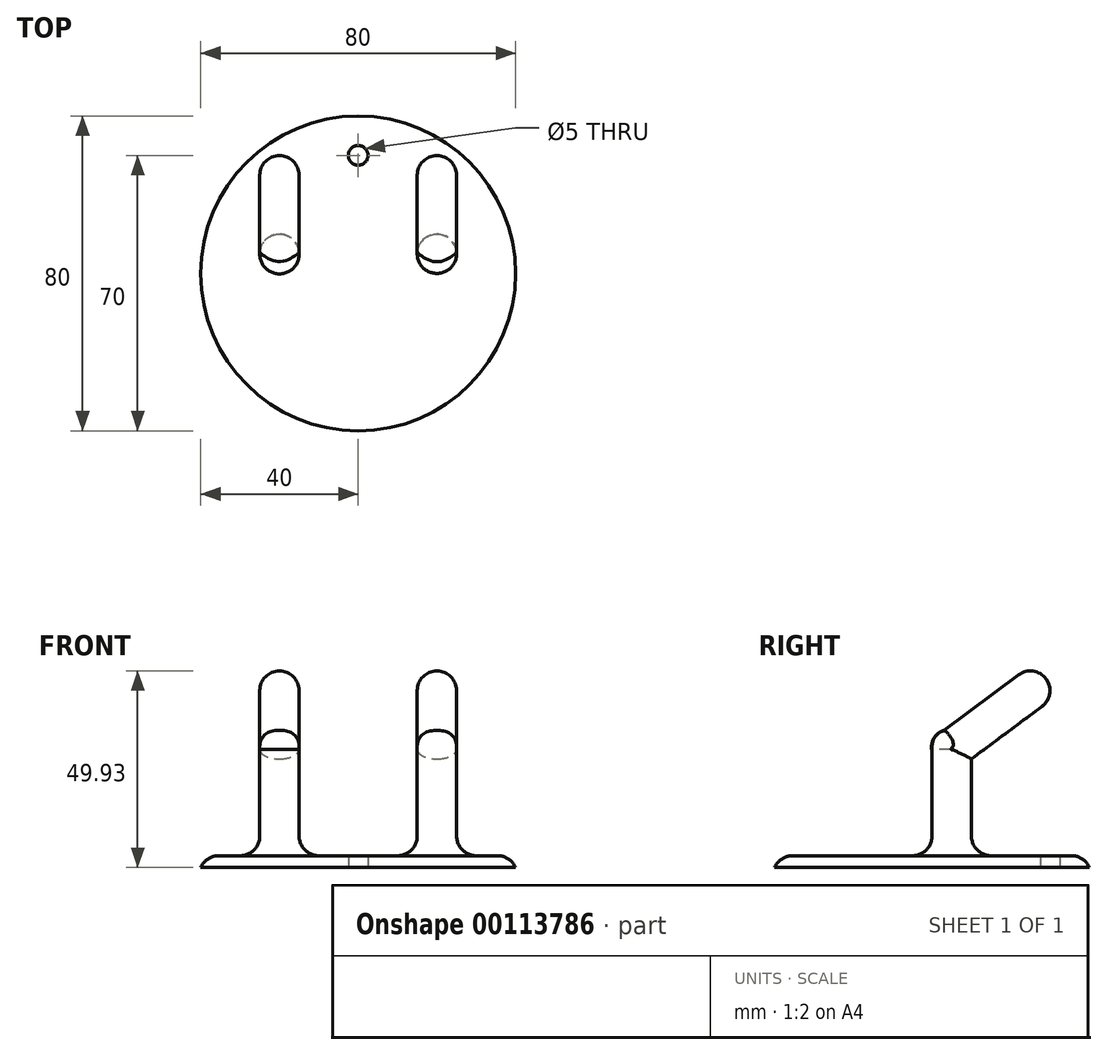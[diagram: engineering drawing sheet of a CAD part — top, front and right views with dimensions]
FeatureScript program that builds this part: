
annotation { "Feature Type Name" : "Feature", "Feature Type Description" : "" }
export const myFeature = defineFeature(function(context is Context, id is Id, definition is map)
    precondition{}
    {
        {
            var Q0;
            Q0=qCreatedBy(makeId("Top.planeOp"),FACE);
            var sketch = newSketch(context, id + "F0", { "sketchPlane" : qUnion([Q0])});
            skCircle(sketch, "E0", {"center": v(0, 0) * mm, "radius": 40 * mm});
            skLineSegment(sketch, "E1", {"start": v(-40, 0) * mm, "end": v(40, 0) * mm});
            skLineSegment(sketch, "E2", {"start": v(-39.69, 5) * mm, "end": v(39.69, 5) * mm});
            skSolve(sketch);
        }
        {
            var Q0;
            {var subQ0=sQuery(id+"F0.wireOp",EDGE,"E2");Q0=makeQuery(id+"F0.imprint","IMPRINT",FACE,{"disambiguationData":[TD([[makeQuery(id+"F0.imprint","IMPRINT",EDGE,{"derivedFrom":subQ0}),1.0]])]});}
            var sketch = newSketch(context, id + "F1", { "sketchPlane" : qUnion([Q0])});
            skCircle(sketch, "E3", {"center": v(-20, 5) * mm, "radius": 5 * mm});
            skCircle(sketch, "E4", {"center": v(20, 5) * mm, "radius": 5 * mm});
            skSolve(sketch);
        }
        {
            var Q0;
            {var subQ0=sQuery(id+"F0.wireOp",EDGE,"E2");Q0=makeQuery(id+"F0.imprint","IMPRINT",FACE,{"disambiguationData":[TD([[makeQuery(id+"F0.imprint","IMPRINT",EDGE,{"derivedFrom":subQ0}),1.0]])]});}
            var sketch = newSketch(context, id + "F2", { "sketchPlane" : qUnion([Q0])});
            skCircle(sketch, "E5", {"center": v(0, 30) * mm, "radius": 2.5 * mm});
            skSolve(sketch);
        }
        {
            var Q0;
            Q0 = qSketchRegion(id + "F0", true);
            extrude(context, id + "F3", {"entities" : qUnion([Q0]), "depth" : 3 * mm});
        }
        {
            var Q0;
            Q0 = qSketchRegion(id + "F1", true);
            extrude(context, id + "F4", {"entities" : qUnion([Q0]), "operationType" : NewBodyOperationType.ADD, "depth" : 30 * mm});
        }
        {
            var Q0;
            Q0 = qSketchRegion(id + "F2", true);
            extrude(context, id + "F5", {"entities" : qUnion([Q0]), "operationType" : NewBodyOperationType.REMOVE, "depth" : 3 * mm});
        }
        {
            var Q0;
            Q0=makeQuery(id+"F4.opExtrude","CAP_FACE",FACE,{"disambiguationData":[OSD([sQuery(id+"F1.wireOp",EDGE,"E3")])],"isStart":false});
            var sketch = newSketch(context, id + "F6", { "sketchPlane" : qUnion([Q0])});
            skLineSegment(sketch, "E6", {"start": v(-25, 4.9) * mm, "end": v(25, 4.9) * mm});
            skSolve(sketch);
        }
        {
            var Q0;
            Q0=makeQuery(id+"F3.opExtrude","CAP_FACE",FACE,{"disambiguationData":[OSD([sQuery(id+"F0.wireOp",EDGE,"E0")])],"isStart":false});
            var sketch = newSketch(context, id + "F7", { "sketchPlane" : qUnion([Q0])});
            skLineSegment(sketch, "E7", {"start": v(-20, 25) * mm, "end": v(-20, 0) * mm});
            skLineSegment(sketch, "E8", {"start": v(20, 10) * mm, "end": v(20, 0) * mm});
            skSolve(sketch);
        }
        {
            var Q0;
            Q0=sQuery(id+"F6.wireOp",VERTEX,"E6.start");
            var Q1;
            Q1=sQuery(id+"F6.wireOp",VERTEX,"E6.end");
            var Q2;
            Q2=sQuery(id+"F7.wireOp",VERTEX,"E7.start");
            cPlane(context, id + "F8", {"entities" : qUnion([Q0, Q1, Q2]), "cplaneType" : CPlaneType.THREE_POINT, "offset" : 25 * mm, "width" : 150 * mm, "height" : 150 * mm});
        }
        {
            var Q0;
            Q0=qCreatedBy(id+"F8.planeOp",FACE);
            var sketch = newSketch(context, id + "F9", { "sketchPlane" : qUnion([Q0])});
            skCircle(sketch, "E9", {"center": v(-20, 21.14) * mm, "radius": 5 * mm});
            skCircle(sketch, "E10", {"center": v(20, 21.14) * mm, "radius": 5 * mm});
            skSolve(sketch);
        }
        {
            var Q0;
            Q0 = qSketchRegion(id + "F9", true);
            extrude(context, id + "F10", {"entities" : qUnion([Q0]), "operationType" : NewBodyOperationType.ADD, "oppositeDirection" : true, "depth" : 30 * mm});
        }
        {
            var Q0;
            {var subQ0=sQuery(id+"F6.wireOp",EDGE,"E6");var subQ1=makeQuery(id+"F4.opExtrude","CAP_EDGE",EDGE,{"disambiguationData":[OSD([sQuery(id+"F1.wireOp",EDGE,"E3")])],"isStart":false});var subQ2=makeQuery(id+"F6.imprint","INTERSECT",VERTEX,{"disambiguationData":[OD(0.0)],"derivedFrom":[subQ1,subQ0]});Q0=makeQuery(id+"F6.imprint","IMPRINT",FACE,{"disambiguationData":[TD([[makeQuery(id+"F6.imprint","IMPRINT",EDGE,{"disambiguationData":[TD([[subQ2,-1.0]])],"derivedFrom":subQ0}),1.0]])]});}
            var sketch = newSketch(context, id + "F11", { "sketchPlane" : qUnion([Q0])});
            skCircle(sketch, "E11", {"center": v(-20, 4.9) * mm, "radius": 5 * mm});
            skCircle(sketch, "E12", {"center": v(20, 5) * mm, "radius": 5 * mm});
            skSolve(sketch);
        }
        {
            var Q0;
            Q0 = qSketchRegion(id + "F11", true);
            extrude(context, id + "F12", {"entities" : qUnion([Q0]), "operationType" : NewBodyOperationType.ADD, "depth" : 5 * mm});
        }
        {
            var Q0;
            Q0=makeQuery(id+"F10.opExtrude","CAP_EDGE",EDGE,{"disambiguationData":[OSD([sQuery(id+"F9.wireOp",EDGE,"E9")])],"isStart":false});
            var Q1;
            Q1=makeQuery(id+"F10.opExtrude","CAP_EDGE",EDGE,{"disambiguationData":[OSD([sQuery(id+"F9.wireOp",EDGE,"E10")])],"isStart":false});
            fillet(context, id + "F13", {"entities" : qUnion([Q0, Q1]), "radius" : 5 * mm, "tangentPropagation" : true, "allowEdgeOverflow" : false});
        }
        {
            var Q0;
            Q0=makeQuery(id+"F4.boolean.opBoolean","INTERSECT",EDGE,{"derivedFrom":[makeQuery(id+"F3.opExtrude","CAP_FACE",FACE,{"disambiguationData":[OSD([sQuery(id+"F0.wireOp",EDGE,"E0")])],"isStart":false}),makeQuery(id+"F4.opExtrude","SWEPT_FACE",FACE,{"disambiguationData":[OSD([sQuery(id+"F1.wireOp",EDGE,"E4")])]})]});
            var Q1;
            Q1=makeQuery(id+"F4.boolean.opBoolean","INTERSECT",EDGE,{"derivedFrom":[makeQuery(id+"F3.opExtrude","CAP_FACE",FACE,{"disambiguationData":[OSD([sQuery(id+"F0.wireOp",EDGE,"E0")])],"isStart":false}),makeQuery(id+"F4.opExtrude","SWEPT_FACE",FACE,{"disambiguationData":[OSD([sQuery(id+"F1.wireOp",EDGE,"E3")])]})]});
            fillet(context, id + "F14", {"entities" : qUnion([Q0, Q1]), "radius" : 5 * mm, "tangentPropagation" : true, "allowEdgeOverflow" : false});
        }
        {
            var Q0;
            Q0=makeQuery(id+"F3.opExtrude","CAP_EDGE",EDGE,{"disambiguationData":[OSD([sQuery(id+"F0.wireOp",EDGE,"E0")])],"isStart":false});
            fillet(context, id + "F15", {"entities" : qUnion([Q0]), "radius" : 5 * mm, "tangentPropagation" : true, "allowEdgeOverflow" : false});
        }
        {
            var Q0;
            Q0=makeQuery(id+"F12.opExtrude","CAP_EDGE",EDGE,{"disambiguationData":[OSD([sQuery(id+"F11.wireOp",EDGE,"E11")])],"isStart":false});
            var Q1;
            Q1=makeQuery(id+"F12.opExtrude","CAP_EDGE",EDGE,{"disambiguationData":[OSD([sQuery(id+"F11.wireOp",EDGE,"E12")])],"isStart":false});
            fillet(context, id + "F16", {"entities" : qUnion([Q0, Q1]), "radius" : 4.25 * mm, "tangentPropagation" : true, "allowEdgeOverflow" : false});
        }
    });
